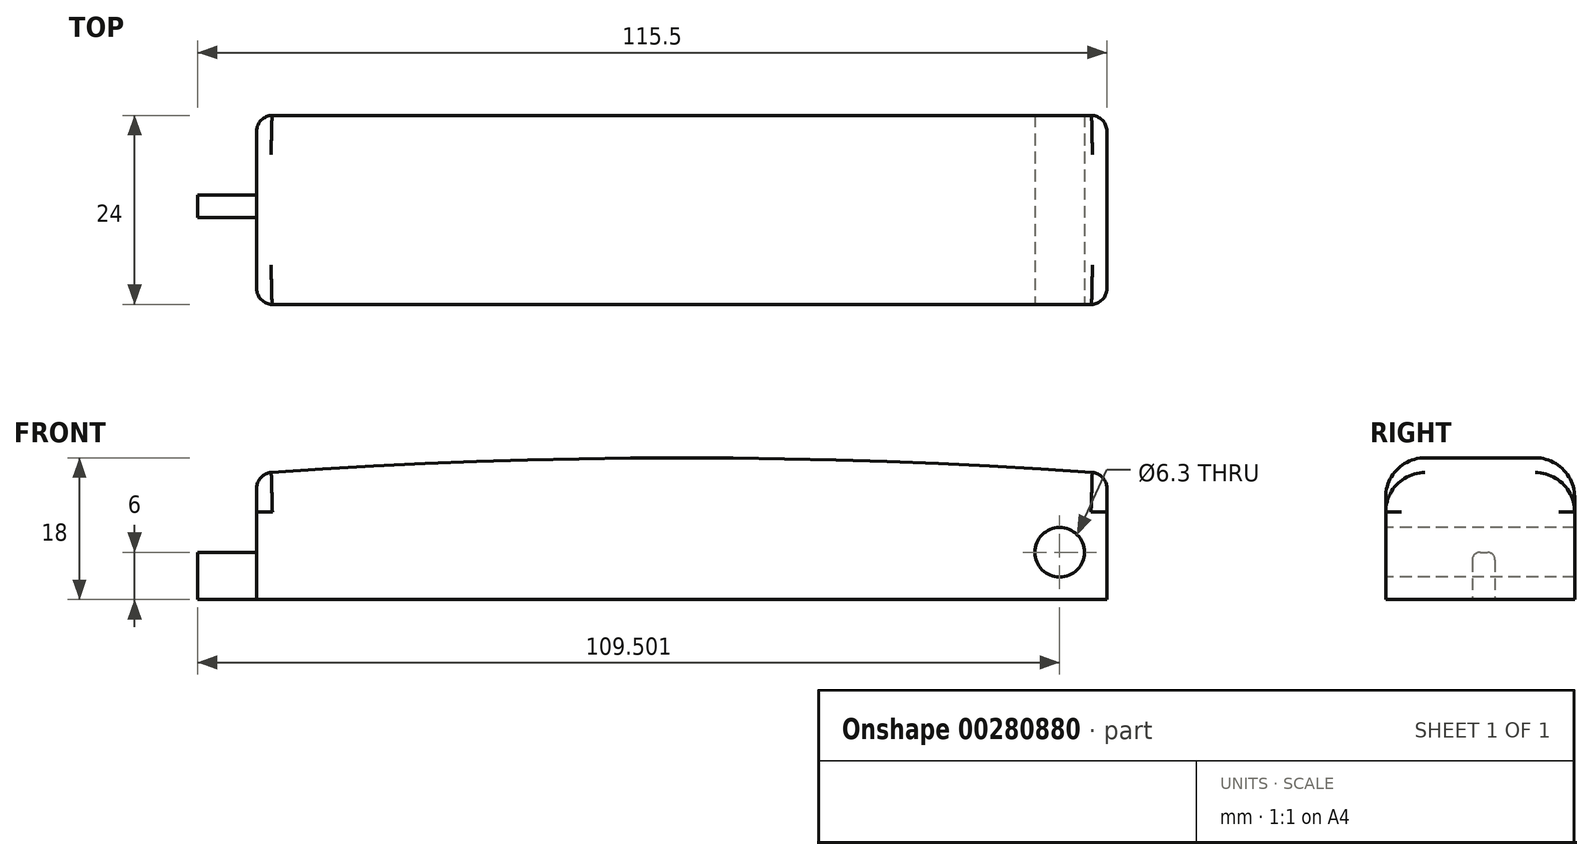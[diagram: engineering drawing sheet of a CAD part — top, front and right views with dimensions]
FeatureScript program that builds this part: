
annotation { "Feature Type Name" : "Feature", "Feature Type Description" : "" }
export const myFeature = defineFeature(function(context is Context, id is Id, definition is map)
    precondition{}
    {
        {
            var Q0;
            Q0=qCreatedBy(makeId("Top.planeOp"),FACE);
            var sketch = newSketch(context, id + "F0", { "sketchPlane" : qUnion([Q0])});
            skLineSegment(sketch, "E0.bottom", {"start": v(-37.96, 5.27) * mm, "end": v(70.04, 5.27) * mm});
            skLineSegment(sketch, "E0.top", {"start": v(-37.96, -18.73) * mm, "end": v(70.04, -18.73) * mm});
            skLineSegment(sketch, "E0.left", {"start": v(-37.96, 5.27) * mm, "end": v(-37.96, -18.73) * mm});
            skLineSegment(sketch, "E0.right", {"start": v(70.04, 5.27) * mm, "end": v(70.04, -18.73) * mm});
            skSolve(sketch);
        }
        {
            var Q0;
            Q0=makeQuery(id+"F0.imprint","IMPRINT",FACE,{"disambiguationData":[TD([[makeQuery(id+"F0.imprint","IMPRINT",EDGE,{"derivedFrom":sQuery(id+"F0.wireOp",EDGE,"E0.bottom")}),-1.0]])]});
            extrude(context, id + "F1", {"entities" : qUnion([Q0]), "depth" : 16 * mm, "offsetDistance" : 25 * mm});
        }
        {
            var Q0;
            Q0=makeQuery(id+"F1.opExtrude","SWEPT_FACE",FACE,{"disambiguationData":[OSD([sQuery(id+"F0.wireOp",EDGE,"E0.top")])]});
            var sketch = newSketch(context, id + "F2", { "sketchPlane" : qUnion([Q0])});
            skArc(sketch, "E1", {"start": v(70.04, 16) * mm, "mid": v(16.04, 18) * mm, "end": v(-37.96, 16) * mm});
            skLineSegment(sketch, "E2", {"start": v(-37.96, 16) * mm, "end": v(70.04, 16) * mm});
            skSolve(sketch);
        }
        {
            var Q0;
            Q0=makeQuery(id+"F2.imprint","IMPRINT",FACE,{"disambiguationData":[TD([[makeQuery(id+"F2.imprint","IMPRINT",EDGE,{"derivedFrom":sQuery(id+"F2.wireOp",EDGE,"E1")}),1.0]])]});
            extrude(context, id + "F3", {"entities" : qUnion([Q0]), "operationType" : NewBodyOperationType.ADD, "depth" : -24 * mm, "offsetDistance" : 25 * mm});
        }
        {
            var Q0;
            {var subQ0=sQuery(id+"F0.wireOp",EDGE,"E0.left");Q0=makeQuery(id+"F3.boolean.opBoolean","MERGE",EDGE,{"derivedFrom":[makeQuery(id+"F1.opExtrude","CAP_EDGE",EDGE,{"disambiguationData":[OSD([subQ0])],"isStart":false}),makeQuery(id+"F3.opExtrude","SWEPT_EDGE",EDGE,{"disambiguationData":[OSD([sQuery(id+"F0.wireOp",EDGE,"E0.top"),subQ0,sQuery(id+"F2.wireOp",EDGE,"E1"),sQuery(id+"F2.wireOp",EDGE,"E2")])]})]});}
            var Q1;
            Q1=makeQuery(id+"F1.opExtrude","SWEPT_EDGE",EDGE,{"disambiguationData":[OSD([sQuery(id+"F0.wireOp",EDGE,"E0.top"),sQuery(id+"F0.wireOp",EDGE,"E0.left")])]});
            var Q2;
            Q2=makeQuery(id+"F1.opExtrude","SWEPT_EDGE",EDGE,{"disambiguationData":[OSD([sQuery(id+"F0.wireOp",EDGE,"E0.bottom"),sQuery(id+"F0.wireOp",EDGE,"E0.left")])]});
            var Q3;
            {var subQ0=sQuery(id+"F0.wireOp",EDGE,"E0.right");Q3=makeQuery(id+"F3.boolean.opBoolean","MERGE",EDGE,{"derivedFrom":[makeQuery(id+"F1.opExtrude","CAP_EDGE",EDGE,{"disambiguationData":[OSD([subQ0])],"isStart":false}),makeQuery(id+"F3.opExtrude","SWEPT_EDGE",EDGE,{"disambiguationData":[OSD([sQuery(id+"F0.wireOp",EDGE,"E0.top"),subQ0,sQuery(id+"F2.wireOp",EDGE,"E1"),sQuery(id+"F2.wireOp",EDGE,"E2")])]})]});}
            var Q4;
            Q4=makeQuery(id+"F1.opExtrude","SWEPT_EDGE",EDGE,{"disambiguationData":[OSD([sQuery(id+"F0.wireOp",EDGE,"E0.top"),sQuery(id+"F0.wireOp",EDGE,"E0.right")])]});
            var Q5;
            Q5=makeQuery(id+"F1.opExtrude","SWEPT_EDGE",EDGE,{"disambiguationData":[OSD([sQuery(id+"F0.wireOp",EDGE,"E0.bottom"),sQuery(id+"F0.wireOp",EDGE,"E0.right")])]});
            fillet(context, id + "F4", {"entities" : qUnion([Q0, Q1, Q2, Q3, Q4, Q5]), "tangentPropagation" : true, "radius" : 2 * mm, "defaultsChanged" : false, "vertexSettings" : [], "allowEdgeOverflow" : false});
        }
        {
            var Q0;
            Q0=makeQuery(id+"F3.opExtrude","CAP_EDGE",EDGE,{"disambiguationData":[OSD([sQuery(id+"F2.wireOp",EDGE,"E1")])],"isStart":false});
            var Q1;
            Q1=makeQuery(id+"F3.opExtrude","CAP_EDGE",EDGE,{"disambiguationData":[OSD([sQuery(id+"F2.wireOp",EDGE,"E1")])],"isStart":true});
            fillet(context, id + "F5", {"entities" : qUnion([Q0, Q1]), "tangentPropagation" : true, "radius" : 5 * mm, "defaultsChanged" : false, "vertexSettings" : [], "allowEdgeOverflow" : false});
        }
        {
            var Q0;
            Q0=makeQuery(id+"F3.boolean.opBoolean","MERGE",FACE,{"derivedFrom":[makeQuery(id+"F1.opExtrude","SWEPT_FACE",FACE,{"disambiguationData":[OSD([sQuery(id+"F0.wireOp",EDGE,"E0.top")])]}),makeQuery(id+"F3.opExtrude","CAP_FACE",FACE,{"disambiguationData":[OSD([sQuery(id+"F2.wireOp",EDGE,"E1"),sQuery(id+"F2.wireOp",EDGE,"E2")])],"isStart":true})]});
            var sketch = newSketch(context, id + "F6", { "sketchPlane" : qUnion([Q0])});
            skCircle(sketch, "E3", {"center": v(64.04, 6) * mm, "radius": 3.15 * mm});
            skSolve(sketch);
        }
        {
            var Q0;
            Q0=makeQuery(id+"F6.imprint","IMPRINT",FACE,{"disambiguationData":[TD([[makeQuery(id+"F6.imprint","IMPRINT",EDGE,{"derivedFrom":sQuery(id+"F6.wireOp",EDGE,"E3")}),1.0]])]});
            extrude(context, id + "F7", {"entities" : qUnion([Q0]), "operationType" : NewBodyOperationType.REMOVE, "oppositeDirection" : true, "depth" : 25 * mm, "offsetDistance" : 25 * mm});
        }
        {
            var Q0;
            Q0=makeQuery(id+"F1.opExtrude","SWEPT_FACE",FACE,{"disambiguationData":[OSD([sQuery(id+"F0.wireOp",EDGE,"E0.left")])]});
            var sketch = newSketch(context, id + "F8", { "sketchPlane" : qUnion([Q0])});
            skLineSegment(sketch, "E4.bottom", {"start": v(7.73, 6) * mm, "end": v(4.83, 6) * mm});
            skLineSegment(sketch, "E4.left", {"start": v(7.73, 6) * mm, "end": v(7.73, 0) * mm});
            skLineSegment(sketch, "E4.right", {"start": v(4.83, 6) * mm, "end": v(4.83, 0) * mm});
            skPoint(sketch, "E4.middle", {"position": v(6.73, 0) * mm});
            skLineSegment(sketch, "E5", {"start": v(4.83, 0) * mm, "end": v(7.73, 0) * mm});
            skSolve(sketch);
        }
        {
            var Q0;
            Q0=makeQuery(id+"F8.imprint","IMPRINT",FACE,{"disambiguationData":[TD([[makeQuery(id+"F8.imprint","IMPRINT",EDGE,{"derivedFrom":sQuery(id+"F8.wireOp",EDGE,"E4.bottom")}),1.0]])]});
            extrude(context, id + "F9", {"entities" : qUnion([Q0]), "operationType" : NewBodyOperationType.ADD, "depth" : 7.5 * mm, "offsetDistance" : 25 * mm});
        }
        {
            var Q0;
            Q0=makeQuery(id+"F9.opExtrude","SWEPT_EDGE",EDGE,{"disambiguationData":[OSD([sQuery(id+"F8.wireOp",EDGE,"E4.bottom"),sQuery(id+"F8.wireOp",EDGE,"E4.left")])]});
            var Q1;
            Q1=makeQuery(id+"F9.opExtrude","SWEPT_EDGE",EDGE,{"disambiguationData":[OSD([sQuery(id+"F8.wireOp",EDGE,"E4.bottom"),sQuery(id+"F8.wireOp",EDGE,"E4.right")])]});
            fillet(context, id + "F10", {"entities" : qUnion([Q0, Q1]), "tangentPropagation" : true, "radius" : 1 * mm, "defaultsChanged" : false, "vertexSettings" : [], "allowEdgeOverflow" : false});
        }
    });
